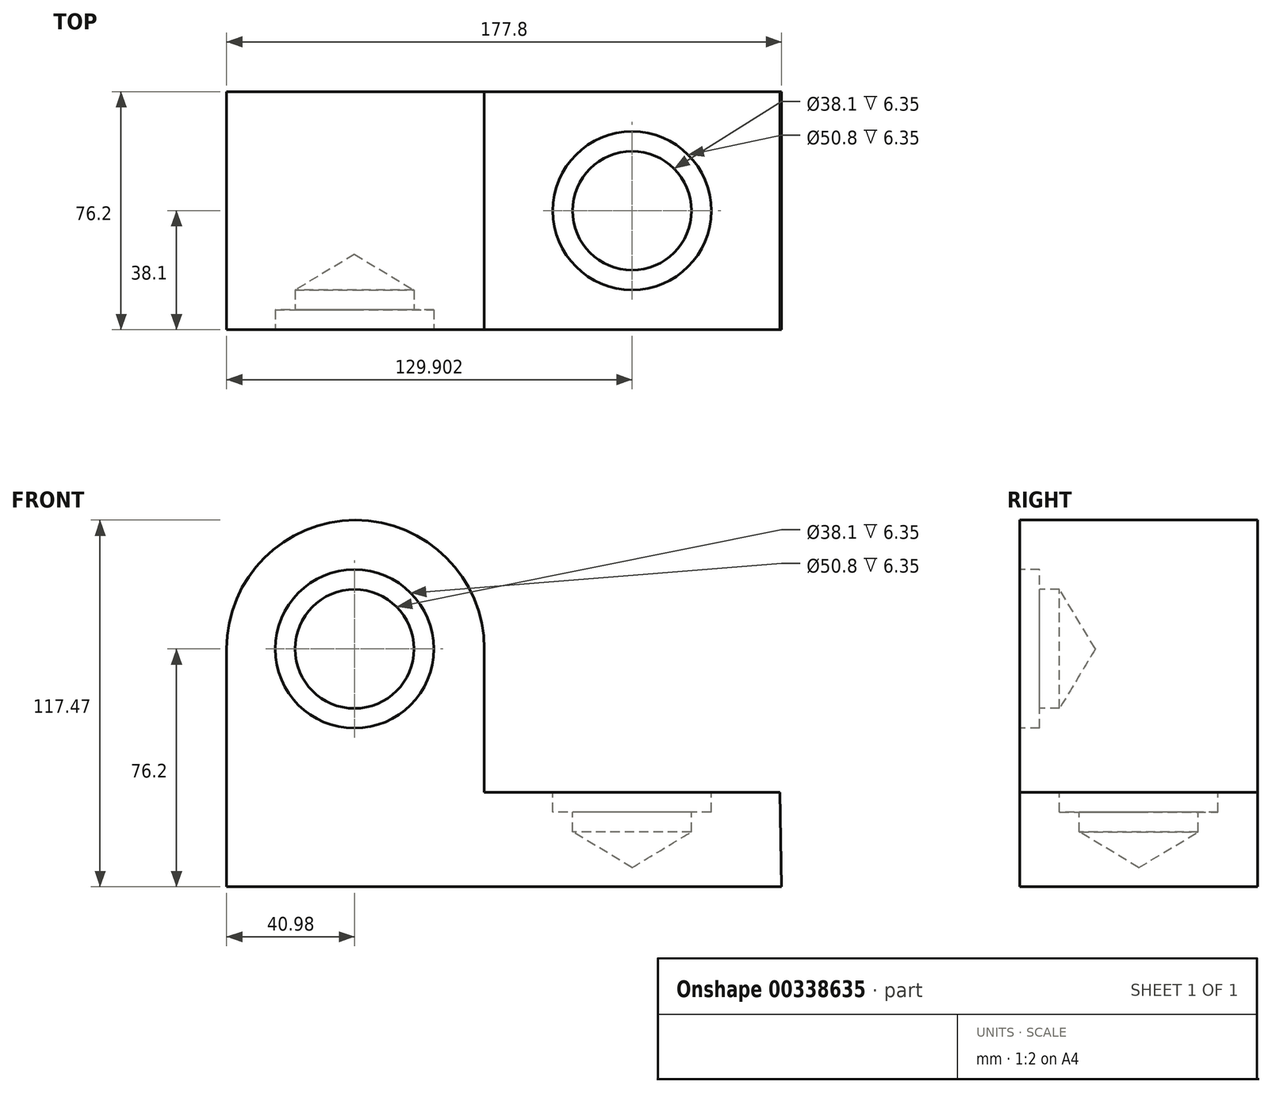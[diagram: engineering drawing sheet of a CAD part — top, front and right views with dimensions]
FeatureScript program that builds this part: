
annotation { "Feature Type Name" : "Feature", "Feature Type Description" : "" }
export const myFeature = defineFeature(function(context is Context, id is Id, definition is map)
    precondition{}
    {
        {
            var Q0;
            Q0=qCreatedBy(makeId("Front.planeOp"),FACE);
            var sketch = newSketch(context, id + "F0", { "sketchPlane" : qUnion([Q0])});
            skCircle(sketch, "E0", {"center": v(0.3, 0) * mm, "radius": 19.05 * mm});
            skCircle(sketch, "E1", {"center": v(0.3, 0) * mm, "radius": 41.28 * mm});
            skLineSegment(sketch, "E2", {"start": v(41.57, 0) * mm, "end": v(41.57, -45.88) * mm});
            skLineSegment(sketch, "E3", {"start": v(41.57, -45.88) * mm, "end": v(136.27, -45.88) * mm});
            skLineSegment(sketch, "E4", {"start": v(136.27, -45.88) * mm, "end": v(136.82, -76.2) * mm});
            skLineSegment(sketch, "E5", {"start": v(136.82, -76.2) * mm, "end": v(-40.98, -76.2) * mm});
            skLineSegment(sketch, "E6", {"start": v(-40.98, 0) * mm, "end": v(-40.98, -76.2) * mm});
            skSolve(sketch);
        }
        {
            var Q0;
            Q0 = qSketchRegion(id + "F0", true);
            var Q1;
            Q1=makeQuery(id+"F0.imprint","IMPRINT",FACE,{"disambiguationData":[TD([[makeQuery(id+"F0.imprint","IMPRINT",EDGE,{"derivedFrom":sQuery(id+"F0.wireOp",EDGE,"E0")}),1.0]])]});
            extrude(context, id + "F1", {"entities" : qUnion([Q0, Q1]), "depth" : 76.2 * mm});
        }
        {
            var Q0;
            Q0=makeQuery(id+"F1.opExtrude","CAP_FACE",FACE,{"disambiguationData":[OSD([sQuery(id+"F0.wireOp",EDGE,"E1"),sQuery(id+"F0.wireOp",EDGE,"E2"),sQuery(id+"F0.wireOp",EDGE,"E3"),sQuery(id+"F0.wireOp",EDGE,"E4"),sQuery(id+"F0.wireOp",EDGE,"E5"),sQuery(id+"F0.wireOp",EDGE,"E6")])],"isStart":false});
            var sketch = newSketch(context, id + "F2", { "sketchPlane" : qUnion([Q0])});
            skCircle(sketch, "E7", {"center": v(0, 0) * mm, "radius": 19.6 * mm});
            skSolve(sketch);
        }
        {
            var Q0;
            Q0=sQuery(id+"F2.wireOp",VERTEX,"E7.center");
            var Q1;
            Q1=makeQuery(id+"F1.opExtrude","SWEPT_BODY",BODY,{"disambiguationData":[OSD([sQuery(id+"F0.wireOp",EDGE,"E1"),sQuery(id+"F0.wireOp",EDGE,"E2"),sQuery(id+"F0.wireOp",EDGE,"E3"),sQuery(id+"F0.wireOp",EDGE,"E4"),sQuery(id+"F0.wireOp",EDGE,"E5"),sQuery(id+"F0.wireOp",EDGE,"E6")])]});
            hole(context, id + "F3", {"style" : HoleStyle.C_BORE, "endStyle" : HoleEndStyle.BLIND, "holeDiameter" : 38.1 * mm, "cBoreDiameter" : 50.8 * mm, "cBoreDepth" : 6.35 * mm, "holeDepth" : 12.7 * mm, "isTappedThrough" : true, "tappedDepth" : 12.7 * mm, "tapClearance" : 3, "locations" : qUnion([Q0]), "scope" : qUnion([Q1])});
        }
        {
            var Q0;
            Q0=makeQuery(id+"F1.opExtrude","SWEPT_FACE",FACE,{"disambiguationData":[OSD([sQuery(id+"F0.wireOp",EDGE,"E3")])]});
            var sketch = newSketch(context, id + "F4", { "sketchPlane" : qUnion([Q0])});
            skCircle(sketch, "E8", {"center": v(88.92, -38.1) * mm, "radius": 20.64 * mm});
            skPoint(sketch, "E8.centerSnap0", {"position": v(88.92, 0) * mm});
            skPoint(sketch, "E8.centerSnap1", {"position": v(136.27, -38.1) * mm});
            skSolve(sketch);
        }
        {
            var Q0;
            Q0=sQuery(id+"F4.wireOp",VERTEX,"E8.center");
            var Q1;
            Q1=makeQuery(id+"F1.opExtrude","SWEPT_BODY",BODY,{"disambiguationData":[OSD([sQuery(id+"F0.wireOp",EDGE,"E1"),sQuery(id+"F0.wireOp",EDGE,"E2"),sQuery(id+"F0.wireOp",EDGE,"E3"),sQuery(id+"F0.wireOp",EDGE,"E4"),sQuery(id+"F0.wireOp",EDGE,"E5"),sQuery(id+"F0.wireOp",EDGE,"E6")])]});
            hole(context, id + "F5", {"style" : HoleStyle.C_BORE, "endStyle" : HoleEndStyle.BLIND, "holeDiameter" : 38.1 * mm, "cBoreDiameter" : 50.8 * mm, "cBoreDepth" : 6.35 * mm, "holeDepth" : 12.7 * mm, "isTappedThrough" : true, "tappedDepth" : 12.7 * mm, "tapClearance" : 3, "locations" : qUnion([Q0]), "scope" : qUnion([Q1])});
        }
    });
